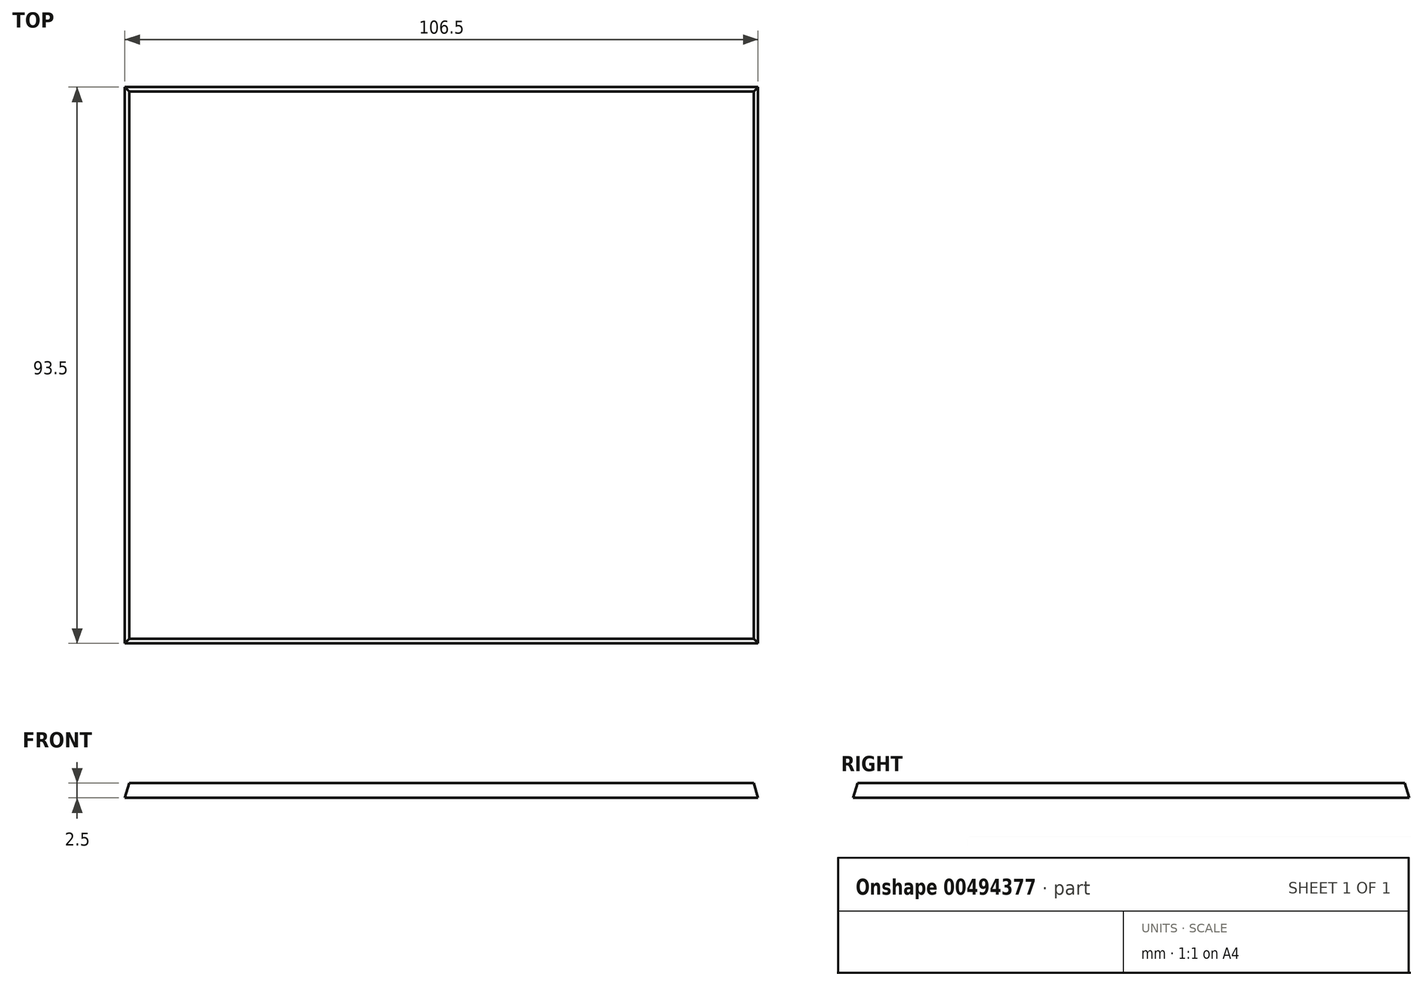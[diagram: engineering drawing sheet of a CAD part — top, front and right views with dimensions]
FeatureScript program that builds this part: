
annotation { "Feature Type Name" : "Feature", "Feature Type Description" : "" }
export const myFeature = defineFeature(function(context is Context, id is Id, definition is map)
    precondition{}
    {
        {
            var Q0;
            Q0=qCreatedBy(makeId("Top.planeOp"),FACE);
            var sketch = newSketch(context, id + "F0", { "sketchPlane" : qUnion([Q0])});
            skLineSegment(sketch, "E0.bottom", {"start": v(54, -47.5) * mm, "end": v(-54, -47.5) * mm});
            skLineSegment(sketch, "E0.top", {"start": v(54, 47.5) * mm, "end": v(-54, 47.5) * mm});
            skLineSegment(sketch, "E0.left", {"start": v(54, -47.5) * mm, "end": v(54, 47.5) * mm});
            skLineSegment(sketch, "E0.right", {"start": v(-54, -47.5) * mm, "end": v(-54, 47.5) * mm});
            skPoint(sketch, "E0.middle", {"position": v(0, 0) * mm});
            skSolve(sketch);
        }
        {
            var Q0;
            Q0=qSketchRegion(id+"F0",true);
            extrude(context, id + "F1", {"entities" : qUnion([Q0]), "depth" : 2.5 * mm});
        }
        {
            var Q0;
            Q0=makeQuery(id+"F1.opExtrude","CAP_EDGE",EDGE,{"disambiguationData":[OSD([sQuery(id+"F0.wireOp",EDGE,"E0.bottom")])],"isStart":false});
            var Q1;
            Q1=makeQuery(id+"F1.opExtrude","CAP_EDGE",EDGE,{"disambiguationData":[OSD([sQuery(id+"F0.wireOp",EDGE,"E0.right")])],"isStart":false});
            var Q2;
            Q2=makeQuery(id+"F1.opExtrude","CAP_EDGE",EDGE,{"disambiguationData":[OSD([sQuery(id+"F0.wireOp",EDGE,"E0.left")])],"isStart":false});
            var Q3;
            Q3=makeQuery(id+"F1.opExtrude","CAP_EDGE",EDGE,{"disambiguationData":[OSD([sQuery(id+"F0.wireOp",EDGE,"E0.top")])],"isStart":false});
            chamfer(context, id + "F2", {"entities" : qUnion([Q0, Q1, Q2, Q3]), "chamferType" : ChamferType.TWO_OFFSETS, "width1" : 5 * mm, "oppositeDirection" : false, "width2" : 1.5 * mm, "tangentPropagation" : true});
        }
    });
